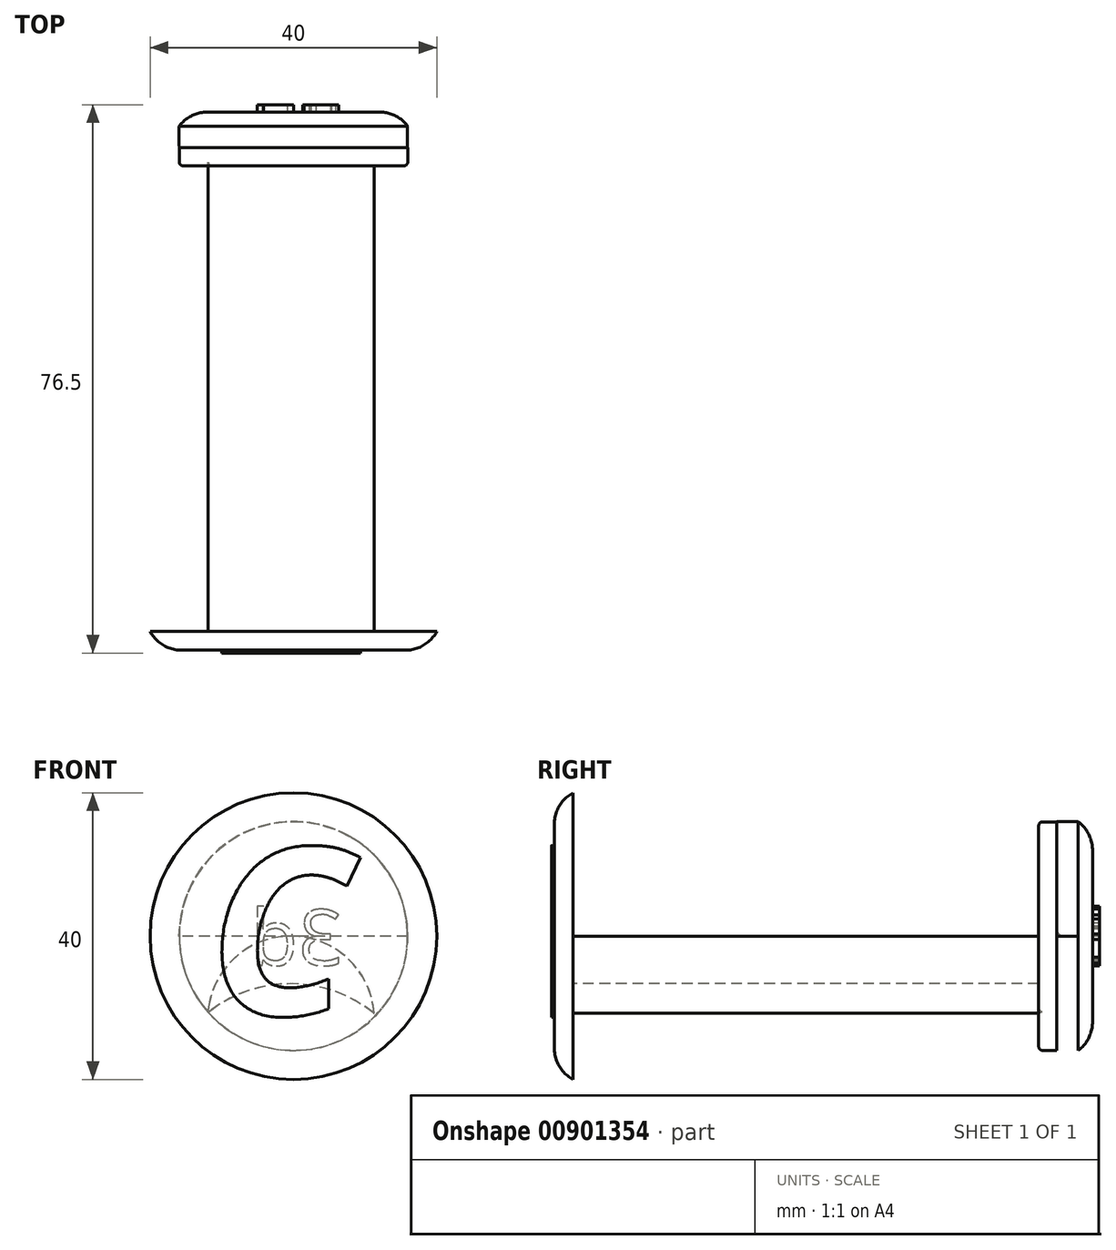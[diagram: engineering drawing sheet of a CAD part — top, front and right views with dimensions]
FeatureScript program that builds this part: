
annotation { "Feature Type Name" : "Feature", "Feature Type Description" : "" }
export const myFeature = defineFeature(function(context is Context, id is Id, definition is map)
    precondition{}
    {
        {
            var Q0;
            Q0=qCreatedBy(makeId("Front.planeOp"),FACE);
            var sketch = newSketch(context, id + "F0", { "sketchPlane" : qUnion([Q0])});
            skCircle(sketch, "E0", {"center": v(0, 0) * mm, "radius": 20 * mm});
            skText(sketch, "E1", { "text": "C", "fontName": "OpenSans-BoldItalic.ttf"});
            const initialGuessF0  = {"E1": [-0.01194, -0.01103, 1, 0, 0.0235]};
            skSetInitialGuess(sketch, initialGuessF0);
            skSolve(sketch);
        }
        {
            var Q0;
            Q0 = qSketchRegion(id + "F0", true);
            extrude(context, id + "F1", {"entities" : qUnion([Q0]), "depth" : 2.6 * mm, "offsetDistance" : 25 * mm});
        }
        {
            var Q0;
            Q0=makeQuery(id+"F0.imprint","IMPRINT",FACE,{"disambiguationData":[TD([[makeQuery(id+"F0.imprint","IMPRINT",EDGE,{"derivedFrom":sQuery(id+"F0.wireOp",EDGE,"E1.sketch_text.stroke-0")}),-1.0]])]});
            extrude(context, id + "F2", {"entities" : qUnion([Q0]), "operationType" : NewBodyOperationType.ADD, "depth" : 3 * mm, "offsetDistance" : 25 * mm});
        }
        {
            var Q0;
            Q0=makeQuery(id+"F0.imprint","IMPRINT",FACE,{"disambiguationData":[TD([[makeQuery(id+"F0.imprint","IMPRINT",EDGE,{"derivedFrom":sQuery(id+"F0.wireOp",EDGE,"E0")}),1.0]])]});
            cPlane(context, id + "F3", {"entities" : qUnion([Q0]), "cplaneType" : CPlaneType.OFFSET, "offset" : 0 * mm, "width" : 150 * mm, "height" : 150 * mm});
        }
        {
            var Q0;
            Q0=qCreatedBy(id+"F3.planeOp",FACE);
            var sketch = newSketch(context, id + "F4", { "sketchPlane" : qUnion([Q0])});
            skArc(sketch, "E2", {"start": v(11.25, -10.77) * mm, "mid": v(-0.3, 0) * mm, "end": v(-11.94, -10.67) * mm});
            skArc(sketch, "E3", {"start": v(11.25, -10.77) * mm, "mid": v(-0.33, -6.64) * mm, "end": v(-11.94, -10.67) * mm});
            skSolve(sketch);
        }
        {
            var Q0;
            Q0 = qSketchRegion(id + "F4", true);
            extrude(context, id + "F5", {"entities" : qUnion([Q0]), "operationType" : NewBodyOperationType.ADD, "oppositeDirection" : true, "depth" : 65 * mm, "offsetDistance" : 25 * mm});
        }
        {
            var Q0;
            Q0=makeQuery(id+"F5.opExtrude","CAP_FACE",FACE,{"disambiguationData":[OSD([sQuery(id+"F4.wireOp",EDGE,"E2"),sQuery(id+"F4.wireOp",EDGE,"E3")])],"isStart":false});
            cPlane(context, id + "F6", {"entities" : qUnion([Q0]), "cplaneType" : CPlaneType.OFFSET, "offset" : 0 * mm, "width" : 150 * mm, "height" : 150 * mm});
        }
        {
            var Q0;
            Q0=qCreatedBy(id+"F6.planeOp",FACE);
            var sketch = newSketch(context, id + "F7", { "sketchPlane" : qUnion([Q0])});
            skCircle(sketch, "E4", {"center": v(0, 0) * mm, "radius": 15.94 * mm});
            skSolve(sketch);
        }
        {
            var Q0;
            Q0 = qSketchRegion(id + "F7", true);
            extrude(context, id + "F8", {"entities" : qUnion([Q0]), "operationType" : NewBodyOperationType.ADD, "depth" : 2.5 * mm, "offsetDistance" : 25 * mm});
        }
        {
            var Q0;
            Q0=makeQuery(id+"F8.opExtrude","CAP_FACE",FACE,{"disambiguationData":[OSD([sQuery(id+"F7.wireOp",EDGE,"E4")])],"isStart":false});
            cPlane(context, id + "F9", {"entities" : qUnion([Q0]), "cplaneType" : CPlaneType.OFFSET, "offset" : 0 * mm, "width" : 150 * mm, "height" : 150 * mm});
        }
        {
            var Q0;
            Q0=qCreatedBy(id+"F9.planeOp",FACE);
            var sketch = newSketch(context, id + "F10", { "sketchPlane" : qUnion([Q0])});
            skLineSegment(sketch, "E5", {"start": v(-15.91, 0) * mm, "end": v(15.95, 0) * mm});
            skArc(sketch, "E6", {"start": v(15.95, 0) * mm, "mid": v(0.02, 15.99) * mm, "end": v(-15.91, 0) * mm});
            skSolve(sketch);
        }
        {
            var Q0;
            Q0 = qSketchRegion(id + "F10", true);
            extrude(context, id + "F11", {"entities" : qUnion([Q0]), "operationType" : NewBodyOperationType.ADD, "depth" : 3 * mm, "offsetDistance" : 25 * mm});
        }
        {
            var Q0;
            Q0=makeQuery(id+"F11.opExtrude","CAP_FACE",FACE,{"disambiguationData":[OSD([sQuery(id+"F10.wireOp",EDGE,"E5"),sQuery(id+"F10.wireOp",EDGE,"E6")])],"isStart":false});
            cPlane(context, id + "F12", {"entities" : qUnion([Q0]), "cplaneType" : CPlaneType.OFFSET, "offset" : 0 * mm, "width" : 150 * mm, "height" : 150 * mm});
        }
        {
            var Q0;
            Q0=qCreatedBy(id+"F12.planeOp",FACE);
            var sketch = newSketch(context, id + "F13", { "sketchPlane" : qUnion([Q0])});
            skCircle(sketch, "E7", {"center": v(0, 0) * mm, "radius": 15.97 * mm});
            skSolve(sketch);
        }
        {
            var Q0;
            Q0 = qSketchRegion(id + "F13", true);
            extrude(context, id + "F14", {"entities" : qUnion([Q0]), "operationType" : NewBodyOperationType.ADD, "depth" : 2 * mm, "offsetDistance" : 25 * mm});
        }
        {
            var Q0;
            Q0=makeQuery(id+"F1.opExtrude","CAP_EDGE",EDGE,{"disambiguationData":[OSD([sQuery(id+"F0.wireOp",EDGE,"E0")])],"isStart":false});
            fillet(context, id + "F15", {"entities" : qUnion([Q0]), "radius" : 5 * mm, "tangentPropagation" : true, "allowEdgeOverflow" : false});
        }
        {
            var Q0;
            Q0=makeQuery(id+"F11.opExtrude","CAP_EDGE",EDGE,{"disambiguationData":[OSD([sQuery(id+"F10.wireOp",EDGE,"E5")])],"isStart":false});
            var Q1;
            {var subQ0=sQuery(id+"F10.wireOp",EDGE,"E5");Q1=makeQuery(id+"F11.boolean.opBoolean","SPLIT",EDGE,{"disambiguationData":[topologyDisambiguationEdgeConnected([makeQuery(id+"F8.opExtrude","CAP_FACE",FACE,{"disambiguationData":[OSD([sQuery(id+"F7.wireOp",EDGE,"E4")])],"isStart":false})])],"derivedFrom":makeQuery(id+"F11.opExtrude","CAP_EDGE",EDGE,{"disambiguationData":[OSD([subQ0])],"isStart":true})});}
            fillet(context, id + "F16", {"entities" : qUnion([Q0, Q1]), "radius" : 1 * mm, "tangentPropagation" : true, "allowEdgeOverflow" : false});
        }
        {
            var Q0;
            Q0=makeQuery(id+"F14.opExtrude","CAP_EDGE",EDGE,{"disambiguationData":[OSD([sQuery(id+"F13.wireOp",EDGE,"E7")])],"isStart":false});
            fillet(context, id + "F17", {"entities" : qUnion([Q0]), "radius" : 5 * mm, "tangentPropagation" : true, "allowEdgeOverflow" : false});
        }
        {
            var Q0;
            Q0=makeQuery(id+"F14.opExtrude","CAP_FACE",FACE,{"disambiguationData":[OSD([sQuery(id+"F13.wireOp",EDGE,"E7")])],"isStart":false});
            cPlane(context, id + "F18", {"entities" : qUnion([Q0]), "cplaneType" : CPlaneType.OFFSET, "offset" : 0 * mm, "width" : 150 * mm, "height" : 150 * mm});
        }
        {
            var Q0;
            Q0=qCreatedBy(id+"F18.planeOp",FACE);
            var sketch = newSketch(context, id + "F19", { "sketchPlane" : qUnion([Q0])});
            skText(sketch, "E8", { "text": "3d", "fontName": "OpenSans-Regular.ttf"});
            const initialGuessF19  = {"E8": [-0.00683, -0.00407, 1, 0, 0.0078]};
            skSetInitialGuess(sketch, initialGuessF19);
            skSolve(sketch);
        }
        {
            var Q0;
            Q0 = qSketchRegion(id + "F19", true);
            extrude(context, id + "F20", {"entities" : qUnion([Q0]), "operationType" : NewBodyOperationType.ADD, "depth" : 1 * mm, "offsetDistance" : 25 * mm});
        }
        {
            var Q0;
            {var subQ0=sQuery(id+"F7.wireOp",EDGE,"E4");Q0=makeQuery(id+"F8.boolean.opBoolean","SPLIT",EDGE,{"disambiguationData":[topologyDisambiguationEdgeConnected([makeQuery(id+"F8.opExtrude","CAP_FACE",FACE,{"disambiguationData":[OSD([subQ0])],"isStart":true})])],"derivedFrom":makeQuery(id+"F8.opExtrude","CAP_EDGE",EDGE,{"disambiguationData":[OSD([subQ0])],"isStart":true})});}
            fillet(context, id + "F21", {"entities" : qUnion([Q0]), "radius" : .5 * mm, "tangentPropagation" : true, "allowEdgeOverflow" : false});
        }
    });
